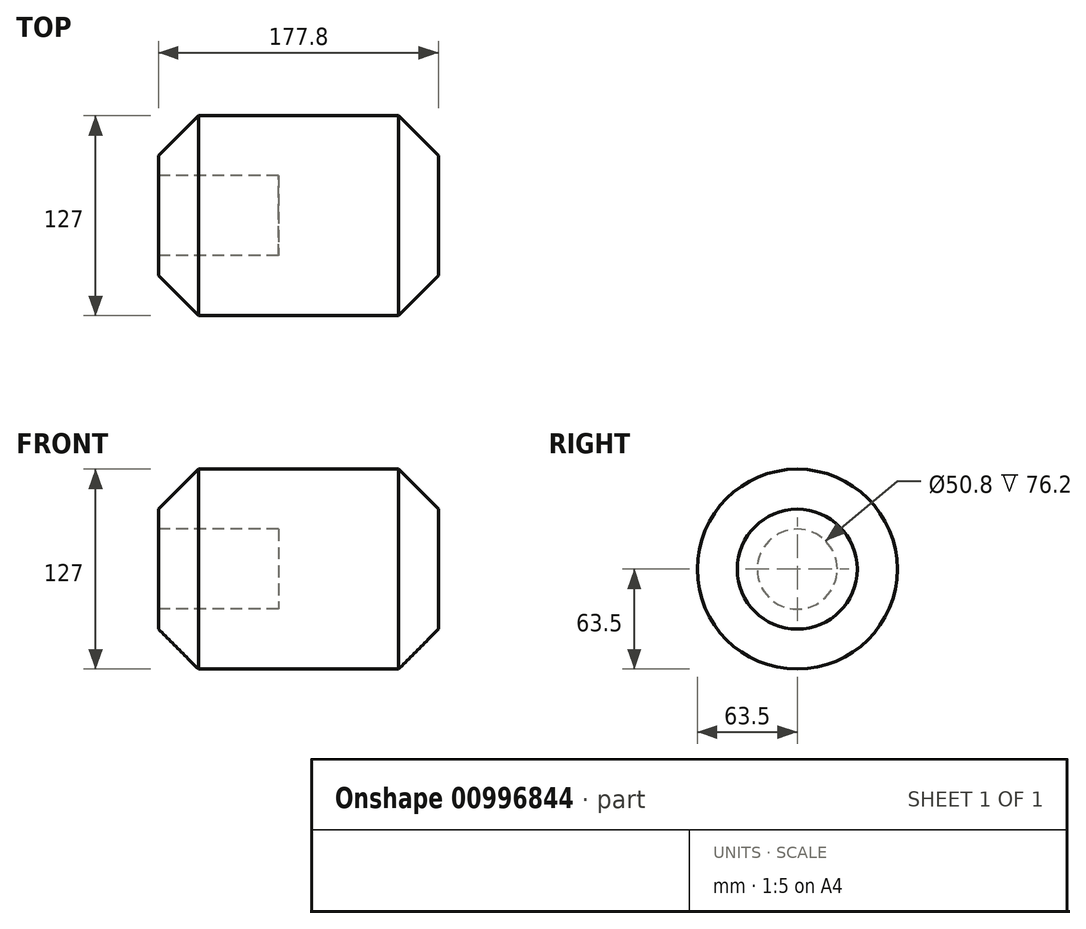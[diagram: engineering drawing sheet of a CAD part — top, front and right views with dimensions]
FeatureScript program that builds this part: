
annotation { "Feature Type Name" : "Feature", "Feature Type Description" : "" }
export const myFeature = defineFeature(function(context is Context, id is Id, definition is map)
    precondition{}
    {
        {
            var Q0;
            Q0=qCreatedBy(makeId("Right.planeOp"),FACE);
            var sketch = newSketch(context, id + "F0", { "sketchPlane" : qUnion([Q0])});
            skCircle(sketch, "E0", {"center": v(0, 0) * mm, "radius": 63.5 * mm});
            skSolve(sketch);
        }
        {
            var Q0;
            Q0 = qSketchRegion(id + "F0", true);
            extrude(context, id + "F1", {"entities" : qUnion([Q0]), "depth" : 177.8 * mm, "offsetDistance" : 25.4 * mm});
        }
        {
            var Q0;
            Q0=makeQuery(id+"F1.opExtrude","CAP_FACE",FACE,{"disambiguationData":[OSD([sQuery(id+"F0.wireOp",EDGE,"E0")])],"isStart":true});
            var sketch = newSketch(context, id + "F2", { "sketchPlane" : qUnion([Q0])});
            skCircle(sketch, "E1", {"center": v(0, 0) * mm, "radius": 25.4 * mm});
            skSolve(sketch);
        }
        {
            var Q0;
            Q0=makeQuery(id+"F2.imprint","IMPRINT",FACE,{"disambiguationData":[TD([[makeQuery(id+"F2.imprint","IMPRINT",EDGE,{"derivedFrom":sQuery(id+"F2.wireOp",EDGE,"E1")}),1.0]])]});
            var Q1;
            Q1=sQuery(id+"F2.wireOp",EDGE,"E1");
            extrude(context, id + "F3", {"entities" : qUnion([Q0]), "operationType" : NewBodyOperationType.REMOVE, "surfaceEntities" : qUnion([Q1]), "oppositeDirection" : true, "depth" : 76.2 * mm, "offsetDistance" : 25.4 * mm});
        }
        {
            var Q0;
            Q0=makeQuery(id+"F1.opExtrude","CAP_EDGE",EDGE,{"disambiguationData":[OSD([sQuery(id+"F0.wireOp",EDGE,"E0")])],"isStart":true});
            var Q1;
            Q1=makeQuery(id+"F1.opExtrude","CAP_EDGE",EDGE,{"disambiguationData":[OSD([sQuery(id+"F0.wireOp",EDGE,"E0")])],"isStart":false});
            var Q2;
            Q2=makeQuery(id+"F1.opExtrude","CAP_FACE",FACE,{"disambiguationData":[OSD([sQuery(id+"F0.wireOp",EDGE,"E0")])],"isStart":false});
            chamfer(context, id + "F4", {"entities" : qUnion([Q0, Q1, Q2]), "width" : 25.4 * mm, "tangentPropagation" : true});
        }
    });
